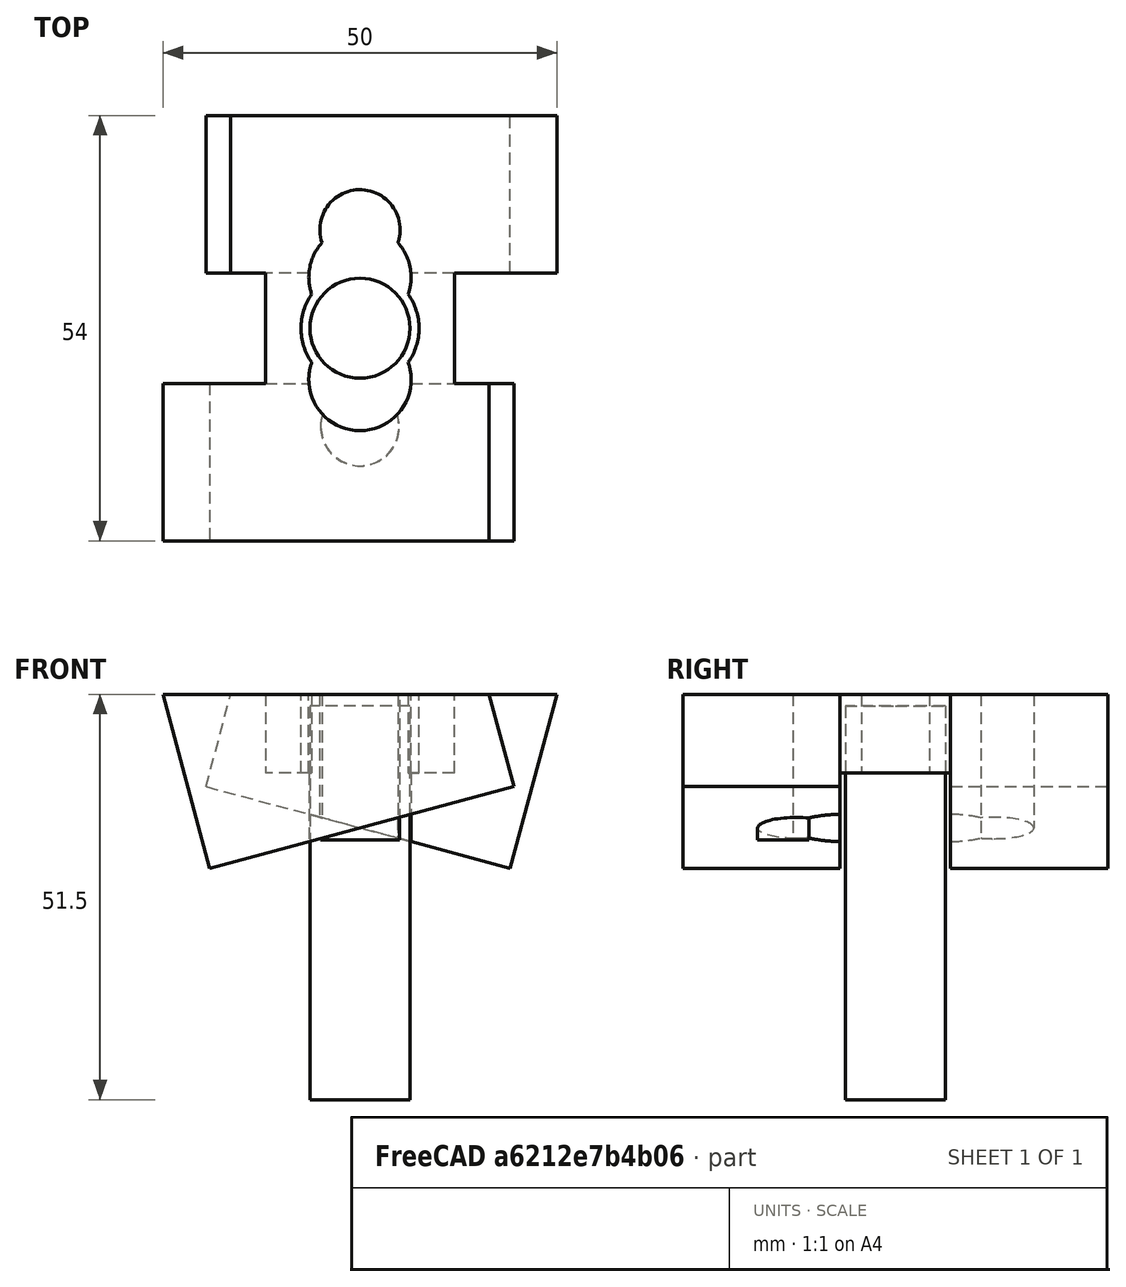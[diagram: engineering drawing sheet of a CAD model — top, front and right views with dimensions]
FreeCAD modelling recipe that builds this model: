
FCSTD DOCUMENT  (FreeCAD 0.20R29410 (Git))
Label: laddleFour2
License: All rights reserved
LicenseURL: http://en.wikipedia.org/wiki/All_rights_reserved
objects: Part::Cylinder×11, Part::MultiFuse×9, Part::Box×4, Part::Cut×4, Part::Feature×1
note: 29 computed .brp shape members not serialized (recipe doc carries the construction recipe); baked Part::Feature solids carry a one-line shape summary decoded from their .brp

FEATURE [Part::Box] Box  label="Cube"
  AttacherType = Attacher::AttachEngine3D
  Height = 30
  Length = 40
  Placement = pos=(-19.5582,7,39.7598) rot=(0,1,0;0.261799rad)
  Width = 20
FEATURE [Part::Box] Box001  label="Cube001"
  AttacherType = Attacher::AttachEngine3D
  Height = 30
  Length = 40
  Placement = pos=(-19.5582,7,39.7598) rot=(0,1,0;0.261799rad)
  Width = 20
FEATURE [Part::Cylinder] Cylinder001
  Angle = 360
  AttacherType = Attacher::AttachEngine3D
  FirstAngle = 0
  Height = 50
  Placement = pos=(0,12.5,0) rot=(0,0,1;0rad)
  Radius = 5
  SecondAngle = 0
FEATURE [Part::Cylinder] Cylinder003  label="bevilPin"
  Angle = 360
  AttacherType = Attacher::AttachEngine3D
  FirstAngle = 0
  Height = 50
  Radius = 6.35
  SecondAngle = 0
FEATURE [Part::Cylinder] Cylinder004  label="bevilPin001"
  Angle = 360
  AttacherType = Attacher::AttachEngine3D
  FirstAngle = 0
  Height = 50
  Radius = 6.35
  SecondAngle = 0
FEATURE [Part::Cylinder] Cylinder005
  Angle = 360
  AttacherType = Attacher::AttachEngine3D
  FirstAngle = 0
  Height = 50
  Placement = pos=(0,12.5,0) rot=(0,0,1;0rad)
  Radius = 5
  SecondAngle = 0
FEATURE [Part::Cylinder] Cylinder006  label="bevilPin002"
  Angle = 360
  AttacherType = Attacher::AttachEngine3D
  FirstAngle = 0
  Height = 50
  Radius = 6.35
  SecondAngle = 0
FEATURE [Part::MultiFuse] Fusion
  Shapes = -> [Cylinder001,Box]
FEATURE [Part::MultiFuse] Fusion001
  Shapes = -> [Fusion,Cylinder004]
FEATURE [Part::MultiFuse] Fusion002
  Shapes = -> [Cylinder005,Box001]
FEATURE [Part::MultiFuse] Fusion003
  Placement = pos=(0,0,0) rot=(0,0,1;3.14159rad)
  Shapes = -> [Fusion002,Cylinder006]
FEATURE [Part::MultiFuse] Fusion004
  Shapes = -> [Fusion003,Fusion001]
FEATURE [Part::Box] Box002  label="Cube002"
  AttacherType = Attacher::AttachEngine3D
  Height = 10
  Length = 24
  Placement = pos=(-12,-13,41.5) rot=(0,0,1;0rad)
  Width = 39
FEATURE [Part::Box] Box003  label="Cube003"
  AttacherType = Attacher::AttachEngine3D
  Height = 20
  Length = 57
  Placement = pos=(-29.5,-29,51.5) rot=(0,0,1;0rad)
  Width = 59
FEATURE [Part::MultiFuse] Fusion005
  Shapes = -> [Box002,Fusion004]
FEATURE [Part::Cut] Cut
  Base = -> Fusion005
  Tool = -> Box003
FEATURE [Part::Cylinder] Cylinder007  label="bevilPin003"
  Angle = 360
  AttacherType = Attacher::AttachEngine3D
  FirstAngle = 0
  Height = 70
  Radius = 7.5
  SecondAngle = 0
FEATURE [Part::Cylinder] Cylinder008
  Angle = 360
  AttacherType = Attacher::AttachEngine3D
  FirstAngle = 0
  Height = 70
  Placement = pos=(0,12.5,0) rot=(0,0,1;0rad)
  Radius = 5.1
  SecondAngle = 0
FEATURE [Part::Cylinder] Cylinder009
  Angle = 360
  AttacherType = Attacher::AttachEngine3D
  FirstAngle = 0
  Height = 70
  Placement = pos=(0,6.5,0) rot=(0,0,1;0rad)
  Radius = 6.5
  SecondAngle = 0
FEATURE [Part::MultiFuse] Fusion006
  Shapes = -> [Cylinder009,Cylinder007]
FEATURE [Part::Cylinder] Cylinder010  label="bevilPin004"
  Angle = 360
  AttacherType = Attacher::AttachEngine3D
  FirstAngle = 0
  Height = 70
  Radius = 7.5
  SecondAngle = 0
FEATURE [Part::Cylinder] Cylinder011
  Angle = 360
  AttacherType = Attacher::AttachEngine3D
  FirstAngle = 0
  Height = 70
  Placement = pos=(0,6.5,0) rot=(0,0,1;0rad)
  Radius = 6.5
  SecondAngle = 0
FEATURE [Part::MultiFuse] Fusion007
  Placement = pos=(0,0,0) rot=(0,0,1;3.14159rad)
  Shapes = -> [Cylinder011,Cylinder010]
FEATURE [Part::MultiFuse] Fusion008
  Shapes = -> [Fusion007,Fusion006]
FEATURE [Part::Cut] Cut001
  Base = -> Cut
  Tool = -> Cylinder008
FEATURE [Part::Cut] Cut002
  Base = -> Cut001
  Tool = -> Fusion008
FEATURE [Part::Cylinder] Cylinder012  label="bevilPin005"
  Angle = 360
  AttacherType = Attacher::AttachEngine3D
  FirstAngle = 0
  Height = 50
  Placement = pos=(0,-12.5,-17) rot=(0,0,1;0rad)
  Radius = 5.1
  SecondAngle = 0
FEATURE [Part::Cut] Cut003
  Base = -> Cut002
  Tool = -> Cylinder012
FEATURE [Part::Feature] Cut003_solid  label="Cut003 (Solid)"
  shape: bbox 50 x 54 x 22.09 mm, 34 faces (baked)
